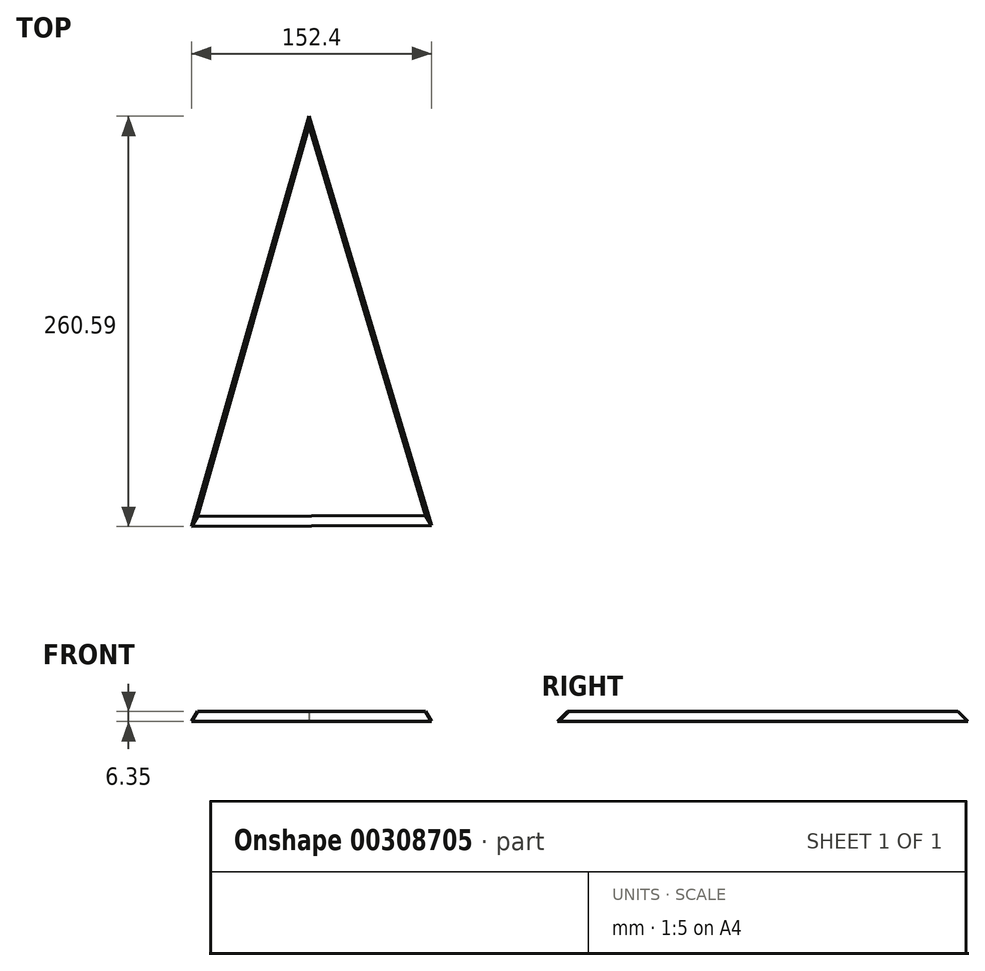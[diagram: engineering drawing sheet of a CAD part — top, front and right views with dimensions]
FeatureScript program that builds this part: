
annotation { "Feature Type Name" : "Feature", "Feature Type Description" : "" }
export const myFeature = defineFeature(function(context is Context, id is Id, definition is map)
    precondition{}
    {
        {
            var Q0;
            Q0=qCreatedBy(makeId("Top.planeOp"),FACE);
            var sketch = newSketch(context, id + "F0", { "sketchPlane" : qUnion([Q0])});
            skCircle(sketch, "E0.cCircle", {"center": v(0, 0) * mm, "radius": 183.96 * mm, "construction": true});
            skLineSegment(sketch, "E0.0", {"start": v(-184.4, 75.14) * mm, "end": v(-77.26, 183.52) * mm});
            skLineSegment(sketch, "E0.1", {"start": v(-77.26, 183.52) * mm, "end": v(75.14, 184.4) * mm});
            skLineSegment(sketch, "E0.2", {"start": v(75.14, 184.4) * mm, "end": v(183.52, 77.26) * mm});
            skLineSegment(sketch, "E0.3", {"start": v(183.52, 77.26) * mm, "end": v(184.4, -75.14) * mm});
            skLineSegment(sketch, "E0.4", {"start": v(184.4, -75.14) * mm, "end": v(77.26, -183.52) * mm});
            skLineSegment(sketch, "E0.5", {"start": v(77.26, -183.52) * mm, "end": v(-75.14, -184.4) * mm});
            skLineSegment(sketch, "E0.6", {"start": v(-75.14, -184.4) * mm, "end": v(-183.52, -77.26) * mm});
            skLineSegment(sketch, "E0.7", {"start": v(-183.52, -77.26) * mm, "end": v(-184.4, 75.14) * mm});
            skPoint(sketch, "E0.0.midPoint", {"position": v(-130.83, 129.33) * mm});
            skSolve(sketch);
        }
        {
            var Q0;
            Q0=makeQuery(id+"F0.imprint","IMPRINT",FACE,{"disambiguationData":[TD([[makeQuery(id+"F0.imprint","IMPRINT",EDGE,{"derivedFrom":sQuery(id+"F0.wireOp",EDGE,"E0.0")}),-1.0]])]});
            extrude(context, id + "F1", {"entities" : qUnion([Q0]), "depth" : 184.15 * mm, "hasDraft" : true, "draftAngle" : 45 * degree, "draftPullDirection" : true});
        }
        {
            var Q0;
            Q0=makeQuery(id+"F1.opExtrude","CAP_FACE",FACE,{"disambiguationData":[OSD([sQuery(id+"F0.wireOp",EDGE,"E0.0"),sQuery(id+"F0.wireOp",EDGE,"E0.1"),sQuery(id+"F0.wireOp",EDGE,"E0.2"),sQuery(id+"F0.wireOp",EDGE,"E0.3"),sQuery(id+"F0.wireOp",EDGE,"E0.4"),sQuery(id+"F0.wireOp",EDGE,"E0.5"),sQuery(id+"F0.wireOp",EDGE,"E0.6"),sQuery(id+"F0.wireOp",EDGE,"E0.7")])],"isStart":true});
            shell(context, id + "F2", {"entities" : qUnion([Q0]), "thickness" : 6.35 * mm});
        }
        {
            var Q0;
            Q0=qCreatedBy(makeId("Top.planeOp"),FACE);
            cPlane(context, id + "F3", {"entities" : qUnion([Q0]), "cplaneType" : CPlaneType.OFFSET, "offset" : 184.15 * mm, "width" : 152.4 * mm, "height" : 152.4 * mm});
        }
        {
            var Q0;
            Q0=qCreatedBy(id+"F3.planeOp",FACE);
            var sketch = newSketch(context, id + "F4", { "sketchPlane" : qUnion([Q0])});
            skLineSegment(sketch, "E1", {"start": v(0, 0) * mm, "end": v(-77.26, 183.52) * mm});
            skLineSegment(sketch, "E2", {"start": v(-77.26, 183.52) * mm, "end": v(75.14, 184.4) * mm});
            skLineSegment(sketch, "E3", {"start": v(75.14, 184.4) * mm, "end": v(0, 0) * mm});
            skLineSegment(sketch, "E4", {"start": v(-77.26, 183.52) * mm, "end": v(-218.75, 184.4) * mm});
            skLineSegment(sketch, "E5", {"start": v(-218.75, 184.4) * mm, "end": v(-221.16, -204.73) * mm});
            skLineSegment(sketch, "E6", {"start": v(-221.16, -204.73) * mm, "end": v(215.23, -207.43) * mm});
            skLineSegment(sketch, "E7", {"start": v(215.23, -207.43) * mm, "end": v(215.23, 184.4) * mm});
            skLineSegment(sketch, "E8", {"start": v(215.23, 184.4) * mm, "end": v(75.14, 184.4) * mm});
            skSolve(sketch);
        }
        {
            var Q0;
            Q0=makeQuery(id+"F4.imprint","IMPRINT",FACE,{"disambiguationData":[TD([[makeQuery(id+"F4.imprint","IMPRINT",EDGE,{"derivedFrom":sQuery(id+"F4.wireOp",EDGE,"E1")}),1.0]])]});
            extrude(context, id + "F5", {"entities" : qUnion([Q0]), "operationType" : NewBodyOperationType.REMOVE, "oppositeDirection" : true, "depth" : 184.15 * mm});
        }
        {
            var Q0;
            Q0=makeQuery(id+"F1.opExtrude","SWEPT_BODY",BODY,{"disambiguationData":[OSD([sQuery(id+"F0.wireOp",EDGE,"E0.0"),sQuery(id+"F0.wireOp",EDGE,"E0.1"),sQuery(id+"F0.wireOp",EDGE,"E0.2"),sQuery(id+"F0.wireOp",EDGE,"E0.3"),sQuery(id+"F0.wireOp",EDGE,"E0.4"),sQuery(id+"F0.wireOp",EDGE,"E0.5"),sQuery(id+"F0.wireOp",EDGE,"E0.6"),sQuery(id+"F0.wireOp",EDGE,"E0.7")])]});
            var Q1;
            Q1=makeQuery(id+"F2.opShell","OFFSET_EDGE",EDGE,{"disambiguationData":[OSD([sQuery(id+"F0.wireOp",EDGE,"E0.1")])]});
            transform(context, id + "F6", {"entities" : qUnion([Q0]), "transformType" : TransformType.ROTATION, "transformAxis" : qUnion([Q1]), "angle" : 45 * degree, "makeCopy" : false});
        }
        {
            var Q0;
            Q0=makeQuery(id+"F1.opExtrude","SWEPT_BODY",BODY,{"disambiguationData":[OSD([sQuery(id+"F0.wireOp",EDGE,"E0.0"),sQuery(id+"F0.wireOp",EDGE,"E0.1"),sQuery(id+"F0.wireOp",EDGE,"E0.2"),sQuery(id+"F0.wireOp",EDGE,"E0.3"),sQuery(id+"F0.wireOp",EDGE,"E0.4"),sQuery(id+"F0.wireOp",EDGE,"E0.5"),sQuery(id+"F0.wireOp",EDGE,"E0.6"),sQuery(id+"F0.wireOp",EDGE,"E0.7")])]});
            var Q1;
            Q1=makeQuery(id+"F1.opExtrude","CAP_EDGE",EDGE,{"disambiguationData":[OSD([sQuery(id+"F0.wireOp",EDGE,"E0.1")])],"isStart":true});
            transform(context, id + "F7", {"entities" : qUnion([Q0]), "transformType" : TransformType.ROTATION, "transformAxis" : qUnion([Q1]), "angle" : 180 * degree, "makeCopy" : false});
        }
        {
            var Q0;
            Q0=makeQuery(id+"F1.opExtrude","SWEPT_BODY",BODY,{"disambiguationData":[OSD([sQuery(id+"F0.wireOp",EDGE,"E0.0"),sQuery(id+"F0.wireOp",EDGE,"E0.1"),sQuery(id+"F0.wireOp",EDGE,"E0.2"),sQuery(id+"F0.wireOp",EDGE,"E0.3"),sQuery(id+"F0.wireOp",EDGE,"E0.4"),sQuery(id+"F0.wireOp",EDGE,"E0.5"),sQuery(id+"F0.wireOp",EDGE,"E0.6"),sQuery(id+"F0.wireOp",EDGE,"E0.7")])]});
            var Q1;
            Q1=makeQuery(id+"F5.boolean.opBoolean","INTERSECT",EDGE,{"derivedFrom":[makeQuery(id+"F2.opShell","OFFSET_FACE",FACE,{"disambiguationData":[OSD([sQuery(id+"F0.wireOp",EDGE,"E0.1")])]}),makeQuery(id+"F5.opExtrude","SWEPT_FACE",FACE,{"disambiguationData":[OSD([sQuery(id+"F4.wireOp",EDGE,"E1")])]})]});
            transform(context, id + "F8", {"entities" : qUnion([Q0]), "transformType" : TransformType.TRANSLATION_DISTANCE, "transformDirection" : qUnion([Q1]), "distance" : 192.53 * mm, "makeCopy" : false});
        }
        {
            var Q0;
            Q0=makeQuery(id+"F1.opExtrude","SWEPT_BODY",BODY,{"disambiguationData":[OSD([sQuery(id+"F0.wireOp",EDGE,"E0.0"),sQuery(id+"F0.wireOp",EDGE,"E0.1"),sQuery(id+"F0.wireOp",EDGE,"E0.2"),sQuery(id+"F0.wireOp",EDGE,"E0.3"),sQuery(id+"F0.wireOp",EDGE,"E0.4"),sQuery(id+"F0.wireOp",EDGE,"E0.5"),sQuery(id+"F0.wireOp",EDGE,"E0.6"),sQuery(id+"F0.wireOp",EDGE,"E0.7")])]});
            var Q1;
            Q1=makeQuery(id+"F1.opExtrude","CAP_EDGE",EDGE,{"disambiguationData":[OSD([sQuery(id+"F0.wireOp",EDGE,"E0.1")])],"isStart":true});
            transform(context, id + "F9", {"entities" : qUnion([Q0]), "transformType" : TransformType.TRANSLATION_DISTANCE, "transformDirection" : qUnion([Q1]), "distance" : 49.28 * mm, "makeCopy" : false});
        }
    });
